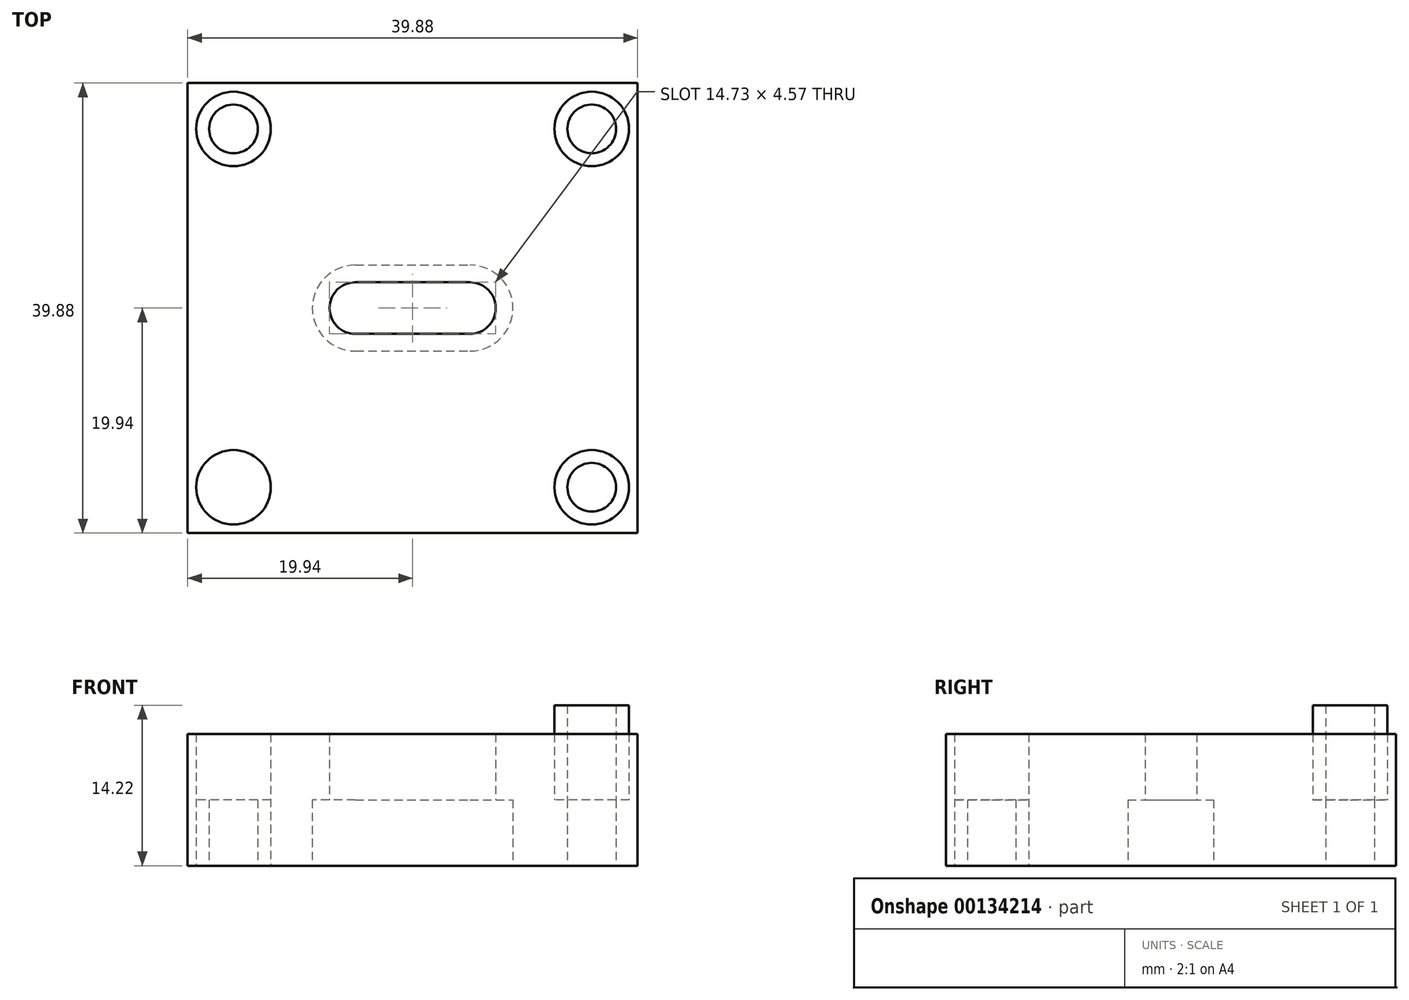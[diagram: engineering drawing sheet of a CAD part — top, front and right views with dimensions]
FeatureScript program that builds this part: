
annotation { "Feature Type Name" : "Feature", "Feature Type Description" : "" }
export const myFeature = defineFeature(function(context is Context, id is Id, definition is map)
    precondition{}
    {
        {
            var Q0;
            Q0=qCreatedBy(makeId("Top.planeOp"),FACE);
            var sketch = newSketch(context, id + "F0", { "sketchPlane" : qUnion([Q0])});
            skLineSegment(sketch, "E0.rect.bottom", {"start": v(19.94, 19.94) * mm, "end": v(-19.94, 19.94) * mm});
            skLineSegment(sketch, "E0.rect.top", {"start": v(19.94, -19.94) * mm, "end": v(-19.94, -19.94) * mm});
            skLineSegment(sketch, "E0.rect.left", {"start": v(19.94, 19.94) * mm, "end": v(19.94, -19.94) * mm});
            skLineSegment(sketch, "E0.rect.right", {"start": v(-19.94, 19.94) * mm, "end": v(-19.94, -19.94) * mm});
            skPoint(sketch, "E0.rect.middle", {"position": v(0, 0) * mm});
            skPoint(sketch, "E1", {"position": v(-15.88, 15.88) * mm});
            skCircle(sketch, "E2", {"center": v(-15.88, 15.88) * mm, "radius": 3.3 * mm});
            skCircle(sketch, "E3", {"center": v(-15.88, 15.88) * mm, "radius": 2.16 * mm});
            skCircle(sketch, "E4.MirrorC", {"center": v(15.88, 15.88) * mm, "radius": 2.16 * mm});
            skCircle(sketch, "E5.MirrorC", {"center": v(15.88, 15.88) * mm, "radius": 3.3 * mm});
            skCircle(sketch, "E6.MirrorC", {"center": v(15.88, -15.88) * mm, "radius": 2.16 * mm});
            skCircle(sketch, "E7.MirrorC", {"center": v(15.88, -15.88) * mm, "radius": 3.3 * mm});
            skCircle(sketch, "E8.MirrorC", {"center": v(-15.88, -15.88) * mm, "radius": 3.3 * mm});
            skCircle(sketch, "E9.MirrorC", {"center": v(-15.88, -15.88) * mm, "radius": 2.16 * mm});
            skLineSegment(sketch, "E10.bottom", {"start": v(19.94, 19.94) * mm, "end": v(7.62, 19.94) * mm});
            skLineSegment(sketch, "E10.top", {"start": v(19.94, -19.94) * mm, "end": v(7.62, -19.94) * mm});
            skLineSegment(sketch, "E10.right", {"start": v(7.62, 19.94) * mm, "end": v(7.62, -19.94) * mm});
            skSolve(sketch);
        }
        {
            var Q0;
            Q0=qSketchRegion(id+"F0",true);
            var Q1;
            {var subQ1=sQuery(id+"F0.wireOp",EDGE,"a0d088e4-a114-4210-b369-51a1f14ee6a4");var subQ3=makeQuery(id+"F0.imprint","IMPRINT",VERTEX,{"derivedFrom":subQ1});Q1=makeQuery(id+"F0.imprint","IMPRINT",FACE,{"disambiguationData":[TD([[makeQuery(id+"F0.imprint","IMPRINT",EDGE,{"disambiguationData":[TD([[subQ3,1.0]])],"derivedFrom":subQ1}),-1.0]])]});}
            var Q2;
            {var subQ0=sQuery(id+"F0.wireOp",EDGE,"gTe1rfOK-hWQo-2Z0q-ZLt7-7Dn1lkIVvu8e");var subQ1=sQuery(id+"F0.wireOp",EDGE,"5fa916a1-46bb-44d0-9b25-f1613092b9c4");var subQ2=makeQuery(id+"F0.imprint","INTERSECT",VERTEX,{"derivedFrom":[subQ1,subQ0]});Q2=makeQuery(id+"F0.imprint","IMPRINT",FACE,{"disambiguationData":[TD([[makeQuery(id+"F0.imprint","IMPRINT",EDGE,{"disambiguationData":[TD([[subQ2,-1.0]])],"derivedFrom":subQ1}),-1.0]])]});}
            var Q3;
            {var subQ0=sQuery(id+"F0.wireOp",EDGE,"K5YmDXpU-GgtS-j2Cr-nMIa-zNqNAAf7L4pf");var subQ1=sQuery(id+"F0.wireOp",EDGE,"f0f4ba78-e869-495a-b748-71ef774c9df5");var subQ2=makeQuery(id+"F0.imprint","INTERSECT",VERTEX,{"derivedFrom":[subQ1,subQ0]});Q3=makeQuery(id+"F0.imprint","IMPRINT",FACE,{"disambiguationData":[TD([[makeQuery(id+"F0.imprint","IMPRINT",EDGE,{"disambiguationData":[TD([[subQ2,1.0]])],"derivedFrom":subQ1}),1.0]])]});}
            var Q4;
            {var subQ0=sQuery(id+"F0.wireOp",EDGE,"K5YmDXpU-GgtS-j2Cr-nMIa-zNqNAAf7L4pf");var subQ1=sQuery(id+"F0.wireOp",EDGE,"5fa916a1-46bb-44d0-9b25-f1613092b9c4");var subQ2=makeQuery(id+"F0.imprint","INTERSECT",VERTEX,{"derivedFrom":[subQ1,subQ0]});Q4=makeQuery(id+"F0.imprint","IMPRINT",FACE,{"disambiguationData":[TD([[makeQuery(id+"F0.imprint","IMPRINT",EDGE,{"disambiguationData":[TD([[subQ2,-1.0]])],"derivedFrom":subQ1}),-1.0]])]});}
            var Q5;
            {var subQ0=sQuery(id+"F0.wireOp",EDGE,"K5YmDXpU-GgtS-j2Cr-nMIa-zNqNAAf7L4pf");var subQ1=sQuery(id+"F0.wireOp",EDGE,"5fa916a1-46bb-44d0-9b25-f1613092b9c4");var subQ2=makeQuery(id+"F0.imprint","INTERSECT",VERTEX,{"derivedFrom":[subQ1,subQ0]});Q5=makeQuery(id+"F0.imprint","IMPRINT",FACE,{"disambiguationData":[TD([[makeQuery(id+"F0.imprint","IMPRINT",EDGE,{"disambiguationData":[TD([[subQ2,-1.0]])],"derivedFrom":subQ1}),1.0]])]});}
            var Q6;
            {var subQ4=sQuery(id+"F0.wireOp",EDGE,"5fa916a1-46bb-44d0-9b25-f1613092b9c4");var subQ6=makeQuery(id+"F0.imprint","INTERSECT",VERTEX,{"derivedFrom":[subQ4,sQuery(id+"F0.wireOp",EDGE,"gTe1rfOK-hWQo-2Z0q-ZLt7-7Dn1lkIVvu8e")]});Q6=makeQuery(id+"F0.imprint","IMPRINT",FACE,{"disambiguationData":[TD([[makeQuery(id+"F0.imprint","IMPRINT",EDGE,{"disambiguationData":[TD([[subQ6,-1.0]])],"derivedFrom":subQ4}),1.0]])]});}
            var Q7;
            {var subQ0=sQuery(id+"F0.wireOp",EDGE,"rkYheQmR-etU9-h3Yq-UIZ2-16BNES9nIO10");Q7=makeQuery(id+"F0.imprint","IMPRINT",FACE,{"disambiguationData":[TD([[makeQuery(id+"F0.imprint","IMPRINT",EDGE,{"derivedFrom":subQ0}),1.0]])]});}
            extrude(context, id + "F1", {"entities" : qUnion([Q0, Q1, Q2, Q3, Q4, Q5, Q6, Q7]), "depth" : 11.68 * mm});
        }
        {
            var Q0;
            Q0=makeQuery(id+"F0.imprint","IMPRINT",FACE,{"disambiguationData":[TD([[makeQuery(id+"F0.imprint","IMPRINT",EDGE,{"derivedFrom":sQuery(id+"F0.wireOp",EDGE,"E2")}),1.0]])]});
            var Q1;
            Q1=makeQuery(id+"F0.imprint","IMPRINT",FACE,{"disambiguationData":[TD([[makeQuery(id+"F0.imprint","IMPRINT",EDGE,{"derivedFrom":sQuery(id+"F0.wireOp",EDGE,"E4.MirrorC")}),1.0]])]});
            var Q2;
            Q2=makeQuery(id+"F0.imprint","IMPRINT",FACE,{"disambiguationData":[TD([[makeQuery(id+"F0.imprint","IMPRINT",EDGE,{"derivedFrom":sQuery(id+"F0.wireOp",EDGE,"E6.MirrorC")}),-1.0]])]});
            var Q3;
            Q3=makeQuery(id+"F0.imprint","IMPRINT",FACE,{"disambiguationData":[TD([[makeQuery(id+"F0.imprint","IMPRINT",EDGE,{"derivedFrom":sQuery(id+"F0.wireOp",EDGE,"E8.MirrorC")}),-1.0]])]});
            extrude(context, id + "F2", {"entities" : qUnion([Q0, Q1, Q2, Q3]), "operationType" : NewBodyOperationType.ADD, "depth" : 5.84 * mm});
        }
        {
            var Q0;
            Q0=makeQuery(id+"F0.imprint","IMPRINT",FACE,{"disambiguationData":[TD([[makeQuery(id+"F0.imprint","IMPRINT",EDGE,{"derivedFrom":sQuery(id+"F0.wireOp",EDGE,"E5.MirrorC")}),1.0]])]});
            extrude(context, id + "F3", {"entities" : qUnion([Q0]), "operationType" : NewBodyOperationType.ADD, "depth" : 14.22 * mm});
        }
        {
            var Q0;
            {var subQ0=sQuery(id+"F0.wireOp",EDGE,"E8.MirrorC");var subQ1=sQuery(id+"F0.wireOp",EDGE,"E7.MirrorC");var subQ2=sQuery(id+"F0.wireOp",EDGE,"E5.MirrorC");var subQ3=sQuery(id+"F0.wireOp",EDGE,"E2");Q0=makeQuery(id+"F2.boolean.opBoolean","MERGE",FACE,{"derivedFrom":[makeQuery(id+"F1.opExtrude","CAP_FACE",FACE,{"disambiguationData":[OSD([sQuery(id+"F0.wireOp",EDGE,"E0.rect.bottom"),sQuery(id+"F0.wireOp",EDGE,"E0.rect.top"),sQuery(id+"F0.wireOp",EDGE,"E0.rect.right"),subQ3,subQ2,subQ1,subQ0,sQuery(id+"F0.wireOp",EDGE,"E10.bottom"),sQuery(id+"F0.wireOp",EDGE,"E10.top"),sQuery(id+"F0.wireOp",EDGE,"E0.rect.left")])],"isStart":true}),makeQuery(id+"F2.opExtrude","CAP_FACE",FACE,{"disambiguationData":[OSD([subQ3,sQuery(id+"F0.wireOp",EDGE,"E3")])],"isStart":true}),makeQuery(id+"F2.opExtrude","CAP_FACE",FACE,{"disambiguationData":[OSD([sQuery(id+"F0.wireOp",EDGE,"E4.MirrorC"),subQ2])],"isStart":true}),makeQuery(id+"F2.opExtrude","CAP_FACE",FACE,{"disambiguationData":[OSD([sQuery(id+"F0.wireOp",EDGE,"E6.MirrorC"),subQ1])],"isStart":true}),makeQuery(id+"F2.opExtrude","CAP_FACE",FACE,{"disambiguationData":[OSD([subQ0,sQuery(id+"F0.wireOp",EDGE,"E9.MirrorC")])],"isStart":true})]});}
            var sketch = newSketch(context, id + "F4", { "sketchPlane" : qUnion([Q0])});
            skCircle(sketch, "E11", {"center": v(5.08, 0) * mm, "radius": 3.81 * mm});
            skCircle(sketch, "E12", {"center": v(5.08, 0) * mm, "radius": 2.29 * mm});
            skLineSegment(sketch, "E13", {"start": v(7.62, 19.94) * mm, "end": v(7.62, -19.94) * mm, "construction": true});
            skCircle(sketch, "E14", {"center": v(-5.08, 0) * mm, "radius": 2.29 * mm});
            skCircle(sketch, "E15", {"center": v(-5.08, 0) * mm, "radius": 3.81 * mm});
            skLineSegment(sketch, "E16", {"start": v(-5.08, 2.29) * mm, "end": v(5.08, 2.29) * mm});
            skLineSegment(sketch, "E17", {"start": v(5.08, -2.29) * mm, "end": v(-5.08, -2.29) * mm});
            skLineSegment(sketch, "E18", {"start": v(-5.08, -3.81) * mm, "end": v(5.08, -3.81) * mm});
            skLineSegment(sketch, "E19", {"start": v(-5.08, 3.8) * mm, "end": v(5.08, 3.8) * mm});
            skSolve(sketch);
        }
        {
            var Q0;
            {var subQ0=sQuery(id+"F4.wireOp",EDGE,"E14");var subQ1=makeQuery(id+"F4.imprint","INTERSECT",VERTEX,{"derivedFrom":[subQ0,sQuery(id+"F4.wireOp",EDGE,"E16")]});Q0=makeQuery(id+"F4.imprint","IMPRINT",FACE,{"disambiguationData":[TD([[makeQuery(id+"F4.imprint","IMPRINT",EDGE,{"disambiguationData":[TD([[subQ1,-1.0]])],"derivedFrom":subQ0}),1.0]])]});}
            var Q1;
            {var subQ0=sQuery(id+"F4.wireOp",EDGE,"E12");var subQ1=makeQuery(id+"F4.imprint","INTERSECT",VERTEX,{"derivedFrom":[subQ0,sQuery(id+"F4.wireOp",EDGE,"E16")]});Q1=makeQuery(id+"F4.imprint","IMPRINT",FACE,{"disambiguationData":[TD([[makeQuery(id+"F4.imprint","IMPRINT",EDGE,{"disambiguationData":[TD([[subQ1,-1.0]])],"derivedFrom":subQ0}),1.0]])]});}
            var Q2;
            {var subQ0=sQuery(id+"F4.wireOp",EDGE,"E16");var subQ1=sQuery(id+"F4.wireOp",EDGE,"E14");var subQ2=makeQuery(id+"F4.imprint","INTERSECT",VERTEX,{"derivedFrom":[subQ1,subQ0]});Q2=makeQuery(id+"F4.imprint","IMPRINT",FACE,{"disambiguationData":[TD([[makeQuery(id+"F4.imprint","IMPRINT",EDGE,{"disambiguationData":[TD([[subQ2,1.0]])],"derivedFrom":subQ1}),-1.0]])]});}
            var Q3;
            {var subQ0=sQuery(id+"F4.wireOp",EDGE,"E16");var subQ1=sQuery(id+"F4.wireOp",EDGE,"E11");var subQ2=makeQuery(id+"F4.imprint","INTERSECT",VERTEX,{"derivedFrom":[subQ1,subQ0]});Q3=makeQuery(id+"F4.imprint","IMPRINT",FACE,{"disambiguationData":[TD([[makeQuery(id+"F4.imprint","IMPRINT",EDGE,{"disambiguationData":[TD([[subQ2,-1.0]])],"derivedFrom":subQ1}),-1.0]])]});}
            var Q4;
            {var subQ0=sQuery(id+"F4.wireOp",EDGE,"E16");var subQ1=sQuery(id+"F4.wireOp",EDGE,"E11");var subQ2=makeQuery(id+"F4.imprint","INTERSECT",VERTEX,{"derivedFrom":[subQ1,subQ0]});Q4=makeQuery(id+"F4.imprint","IMPRINT",FACE,{"disambiguationData":[TD([[makeQuery(id+"F4.imprint","IMPRINT",EDGE,{"disambiguationData":[TD([[subQ2,-1.0]])],"derivedFrom":subQ1}),1.0]])]});}
            extrude(context, id + "F5", {"entities" : qUnion([Q0, Q1, Q2, Q3, Q4]), "operationType" : NewBodyOperationType.REMOVE, "oppositeDirection" : true, "depth" : 25.4 * mm});
        }
        {
            var Q0;
            {var subQ0=sQuery(id+"F4.wireOp",EDGE,"E16");var subQ1=sQuery(id+"F4.wireOp",EDGE,"E14");var subQ2=makeQuery(id+"F4.imprint","INTERSECT",VERTEX,{"derivedFrom":[subQ1,subQ0]});Q0=makeQuery(id+"F4.imprint","IMPRINT",FACE,{"disambiguationData":[TD([[makeQuery(id+"F4.imprint","IMPRINT",EDGE,{"disambiguationData":[TD([[subQ2,1.0]])],"derivedFrom":subQ1}),-1.0]])]});}
            var Q1;
            {var subQ3=sQuery(id+"F4.wireOp",EDGE,"E16");var subQ4=sQuery(id+"F4.wireOp",EDGE,"E14");var subQ5=makeQuery(id+"F4.imprint","INTERSECT",VERTEX,{"derivedFrom":[subQ4,subQ3]});Q1=makeQuery(id+"F4.imprint","IMPRINT",FACE,{"disambiguationData":[TD([[makeQuery(id+"F4.imprint","IMPRINT",EDGE,{"disambiguationData":[TD([[subQ5,-1.0]])],"derivedFrom":subQ4}),-1.0]])]});}
            var Q2;
            {var subQ0=sQuery(id+"F4.wireOp",EDGE,"E19");Q2=makeQuery(id+"F4.imprint","IMPRINT",FACE,{"disambiguationData":[TD([[makeQuery(id+"F4.imprint","IMPRINT",EDGE,{"derivedFrom":subQ0}),-1.0]])]});}
            var Q3;
            {var subQ0=sQuery(id+"F4.wireOp",EDGE,"E16");var subQ1=sQuery(id+"F4.wireOp",EDGE,"E11");var subQ2=makeQuery(id+"F4.imprint","INTERSECT",VERTEX,{"derivedFrom":[subQ1,subQ0]});Q3=makeQuery(id+"F4.imprint","IMPRINT",FACE,{"disambiguationData":[TD([[makeQuery(id+"F4.imprint","IMPRINT",EDGE,{"disambiguationData":[TD([[subQ2,-1.0]])],"derivedFrom":subQ1}),-1.0]])]});}
            var Q4;
            {var subQ0=sQuery(id+"F4.wireOp",EDGE,"E16");var subQ1=sQuery(id+"F4.wireOp",EDGE,"E11");var subQ2=makeQuery(id+"F4.imprint","INTERSECT",VERTEX,{"derivedFrom":[subQ1,subQ0]});Q4=makeQuery(id+"F4.imprint","IMPRINT",FACE,{"disambiguationData":[TD([[makeQuery(id+"F4.imprint","IMPRINT",EDGE,{"disambiguationData":[TD([[subQ2,-1.0]])],"derivedFrom":subQ1}),1.0]])]});}
            var Q5;
            {var subQ5=sQuery(id+"F4.wireOp",EDGE,"E11");var subQ7=makeQuery(id+"F4.imprint","INTERSECT",VERTEX,{"derivedFrom":[subQ5,sQuery(id+"F4.wireOp",EDGE,"E19")]});Q5=makeQuery(id+"F4.imprint","IMPRINT",FACE,{"disambiguationData":[TD([[makeQuery(id+"F4.imprint","IMPRINT",EDGE,{"disambiguationData":[TD([[subQ7,-1.0]])],"derivedFrom":subQ5}),1.0]])]});}
            var Q6;
            {var subQ0=sQuery(id+"F4.wireOp",EDGE,"E18");Q6=makeQuery(id+"F4.imprint","IMPRINT",FACE,{"disambiguationData":[TD([[makeQuery(id+"F4.imprint","IMPRINT",EDGE,{"derivedFrom":subQ0}),1.0]])]});}
            extrude(context, id + "F6", {"entities" : qUnion([Q0, Q1, Q2, Q3, Q4, Q5, Q6]), "operationType" : NewBodyOperationType.REMOVE, "oppositeDirection" : true, "depth" : 5.84 * mm});
        }
    });
